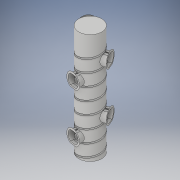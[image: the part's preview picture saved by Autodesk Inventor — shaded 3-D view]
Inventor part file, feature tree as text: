
AUTODESK INVENTOR PART (.ipt)
format: ipt  version: 2017 (Build 210142000, 142)  size: 1,848,320 bytes
history: native  units: in
note: dims shown in document units (in); Inventor stores cm internally (conversion verified against a paired STEP export)
features: extrude x32, sketch x26, other x18, loft x6, shell x1, plane x1
ambient origin geometry x8: Origin, YZ Plane, XZ Plane, XY Plane, X Axis, Y Axis, Z Axis, Center Point
bodies: Solid4 (feature_tree), Solid5 (feature_tree), Solid6 (feature_tree), Solid7 (feature_tree), Solid8 (feature_tree), Solid9 (feature_tree), Solid10 (feature_tree)
feature tree (84):
  shell  "shell and ramp"  Thickness=15.0in
  extrude  "outer cassing"  Depth=72.0in TaperAngle=0.0deg
  extrude  "bottom"  Depth=3.5in
  sketch  "Sketch2"  dims[d40=1.0in d41=0.0in d44=3.5in]
  other  "Work Axis1"
  other  "ramp"
  other  "ramp light"
  other  "top floor fill workplane"
  extrude  "top floor fill"  Depth=0.5in
  sketch  "Sketch5"  dims[d55=3.0in]
  other  "railing complete"
  other  "light ramp to complete"
  extrude  "top cap"  Depth=9.0in
  plane  "workplane sketch"
  other  "connection plane 1"
  other  "connection plane 2"
  other  "connection workplane 3"
  sketch  "Sketch19"  dims[d64=8.0in d65=1.0in d66=3.1201in d67=0.0in d68=90.0deg d69=90.0deg d70=0.0in d71=0.0in d146=9.0in]
  extrude  "bottom connection"  TaperAngle=90.0deg  [1 undecoded]
  extrude  "bottom connect to case"  TaperAngle=90.0deg  [1 undecoded]
  extrude  "connection cut"  Depth=1.0in TaperAngle=0.0deg
  extrude  "light bottom"  Depth=2.6875in TaperAngle=0.0deg
  sketch  "Sketch20"  dims[d147=1.1811in d149=360.0deg d151=90.0deg]
  extrude  "connetion 2"  Depth=1.0in TaperAngle=0.0deg
  extrude  "connection to case 2"  Depth=1.0in TaperAngle=0.0deg
  extrude  "connection cut 2"  Depth=20.15in
  extrude  "light 2"  Depth=1.0in TaperAngle=0.0deg
  loft  "connection ramp 2"
  sketch  "Sketch22"  dims[d152=90.0deg d153=90.0deg]
  extrude  "connection 3"  Depth=1.0in TaperAngle=0.0deg
  extrude  "connection to case 3"  Depth=52.15in
  extrude  "connection cut 3"  Depth=1.0in TaperAngle=0.0deg
  extrude  "light 3"  Depth=6.6667in
  loft  "connetion ramp 3"
  sketch  "Sketch23"  dims[d154=6.6667in d155=4.0in d156=1.0in d157=4.8944in d158=1.0in d159=0.0in]
  extrude  "connection 4"  TaperAngle=0.0deg  [1 undecoded]
  extrude  "connection to case 4"  Depth=1.0in TaperAngle=0.0deg
  extrude  "connection cut 4"  Depth=0.5833in
  extrude  "light 4"  TaperAngle=90.0deg  [1 undecoded]
  loft  "connection ramp 4"
  sketch  "Sketch24"  dims[d160=1.0in d161=0.0in d162=2.6875in d163=0.0in]
  extrude  "connection 5"  TaperAngle=0.0deg  [1 undecoded]
  extrude  "connection to case 5"  TaperAngle=0.0deg  [1 undecoded]
  extrude  "connection cut 5"  Depth=1.0in
  extrude  "light 5"  Depth=1.0in
  loft  "connection ramp 5"
  sketch  "Sketch25"  dims[d164=9.48in]
  extrude  "connection 6"  TaperAngle=0.0deg  [1 undecoded]
  extrude  "connection to case 6"  Depth=1.0in
  extrude  "connection cut 6"  TaperAngle=0.0deg  [1 undecoded]
  extrude  "light 6"  TaperAngle=0.0deg  [1 undecoded]
  loft  "connection ramp 6"
  sketch  "Sketch26"  dims[d165=6.6667in d166=4.0in d167=1.0in d168=4.8944in d169=1.0in d170=0.0in d171=1.0in d172=0.0in]
  extrude  "connection 7"  TaperAngle=0.0deg  [1 undecoded]
  extrude  "connection to case 7"  TaperAngle=0.0deg  [1 undecoded]
  extrude  "connection cut 7"  Depth=1.0in
  extrude  "light 7"  TaperAngle=0.0deg  [1 undecoded]
  loft  "connection ramp 7"
  other  "Delete outer case"
  sketch  "Sketch1"  dims[d1=16.0in d2=72.0in d3=0.0in]
  sketch  "Sketch4"  dims[d53=3.0in d54=0.5in]
  sketch  "Sketch27"  dims[d173=2.625in d174=0.0in]
  sketch  "Sketch28"  dims[d178=6.6667in d179=4.0in d180=1.0in d181=4.8944in d182=1.0in d183=0.0in d184=1.0in d185=0.0in]
  other  "light railing"
  other  "light railing complete"
  sketch  "Sketch29"  dims[d186=1.0in d187=0.0in d188=20.15in]
  other  "Edges1"
  sketch  "Sketch30"  dims[d189=30.81in]
  other  "Edges2"
  sketch  "Sketch31"  dims[d190=6.6667in d191=4.0in d192=1.0in d193=4.8944in d194=1.0in d195=0.0in d196=1.0in d197=0.0in]
  other  "Edges3"
  sketch  "Sketch32"  dims[d198=1.0in d199=0.0in d200=41.48in]
  other  "Edges4"
  sketch  "Sketch33"  dims[d201=6.6667in d202=4.0in d203=1.0in d204=4.8944in d205=1.0in d206=0.0in d207=1.0in d208=0.0in]
  other  "Edges5"
  sketch  "Sketch35"  dims[d209=1.0in d210=0.0in d211=52.15in]
  other  "Edges6"
  sketch  "Sketch36"  dims[d213=6.6667in d214=4.0in d215=1.0in d216=4.8944in d217=1.0in d218=0.0in d219=1.0in d220=0.0in]
  sketch  "Sketch37"  dims[d221=1.0in d222=0.0in d228=6.6667in d229=4.0in d230=1.0in d231=4.8944in]
  sketch  "Sketch38"  dims[d232=62.8in d233=1.0in d234=0.0in]
  sketch  "Sketch39"  dims[d237=1.0in d238=0.0in d239=0.0in]
  sketch  "Sketch40"  dims[d240=1.0in d241=0.0in d242=1.0in d243=0.0in]
  sketch  "Sketch41"  dims[d244=1.0in d245=0.0in d253=0.5833in d254=0.0625in d255=0.0625in d256=0.125in]
  sketch  "Sketch42"  dims[d257=2.0in d268=0.25in d269=0.125in d270=45.0deg d271=0.0892in d272=0.0884in d273=8.0in d274=1.0in d275=3.1201in d276=0.0in d277=90.0deg d278=90.0deg d279=0.0in d280=0.0in d308=3.0in d309=0.5in d310=3.0in d311=0.5833in d312=0.0625in d313=0.0625in d315=0.25in d316=0.125in d317=45.0deg d318=0.0892in d319=0.0884in d320=0.125in d321=90.0deg d322=90.0deg d323=0.0in d324=90.0deg d325=0.0in d326=90.0deg d327=1.0in d329=1.0in d330=0.0in d331=90.0deg d332=0.0in d333=90.0deg d335=1.0in d336=0.0in d337=90.0deg d338=0.0in d339=90.0deg d340=1.0in d341=0.0in d342=90.0deg d343=0.0in d344=90.0deg d346=1.0in d347=0.0in d348=90.0deg d349=0.0in d350=90.0deg d353=1.0in d354=0.0in d355=90.0deg d356=0.0in d357=90.0deg d367=0.5833in d368=0.0625in d369=0.0625in d370=0.25in d371=0.125in d372=0.0892in d373=0.0884in d374=0.125in d375=0.5833in d376=0.0625in d377=0.0625in d378=0.125in d379=1.0in d380=0.0in d381=0.5833in d382=0.0625in d383=0.0625in d384=0.125in d385=0.25in d386=0.125in d387=45.0deg d388=0.0892in d389=0.0884in d390=1.0in d391=0.0in d392=0.5833in d393=0.0625in d394=0.0625in d395=0.125in d396=0.25in d397=0.125in d398=45.0deg d399=0.0892in d400=0.0884in d401=1.0in d402=0.0in d403=0.5833in d404=0.0625in d405=0.0625in d406=0.125in d407=0.25in d408=0.125in d409=45.0deg d410=0.0892in d411=0.0884in d412=1.0in d413=0.0in d414=0.5833in d415=0.0625in d416=0.0625in d417=0.125in d418=0.25in d419=0.125in d420=45.0deg d421=0.0892in d422=0.0884in d423=1.0in d424=0.0in d425=0.5833in d426=0.0625in d427=0.0625in d428=0.125in d429=0.25in d430=0.125in d431=45.0deg d432=0.0892in d433=0.0884in d434=1.0in d435=0.0in d436=0.25in d437=0.125in d438=45.0deg d439=0.0892in d440=0.0884in d441=0.5833in d442=0.0625in d443=0.0625in d444=0.125in d445=1.0in d446=0.0in]
note: 12 required parameter values undecoded (feature->parameter linkage not recoverable at this tier; creation-order binding heuristic only, values carry confidence <= 0.55)
